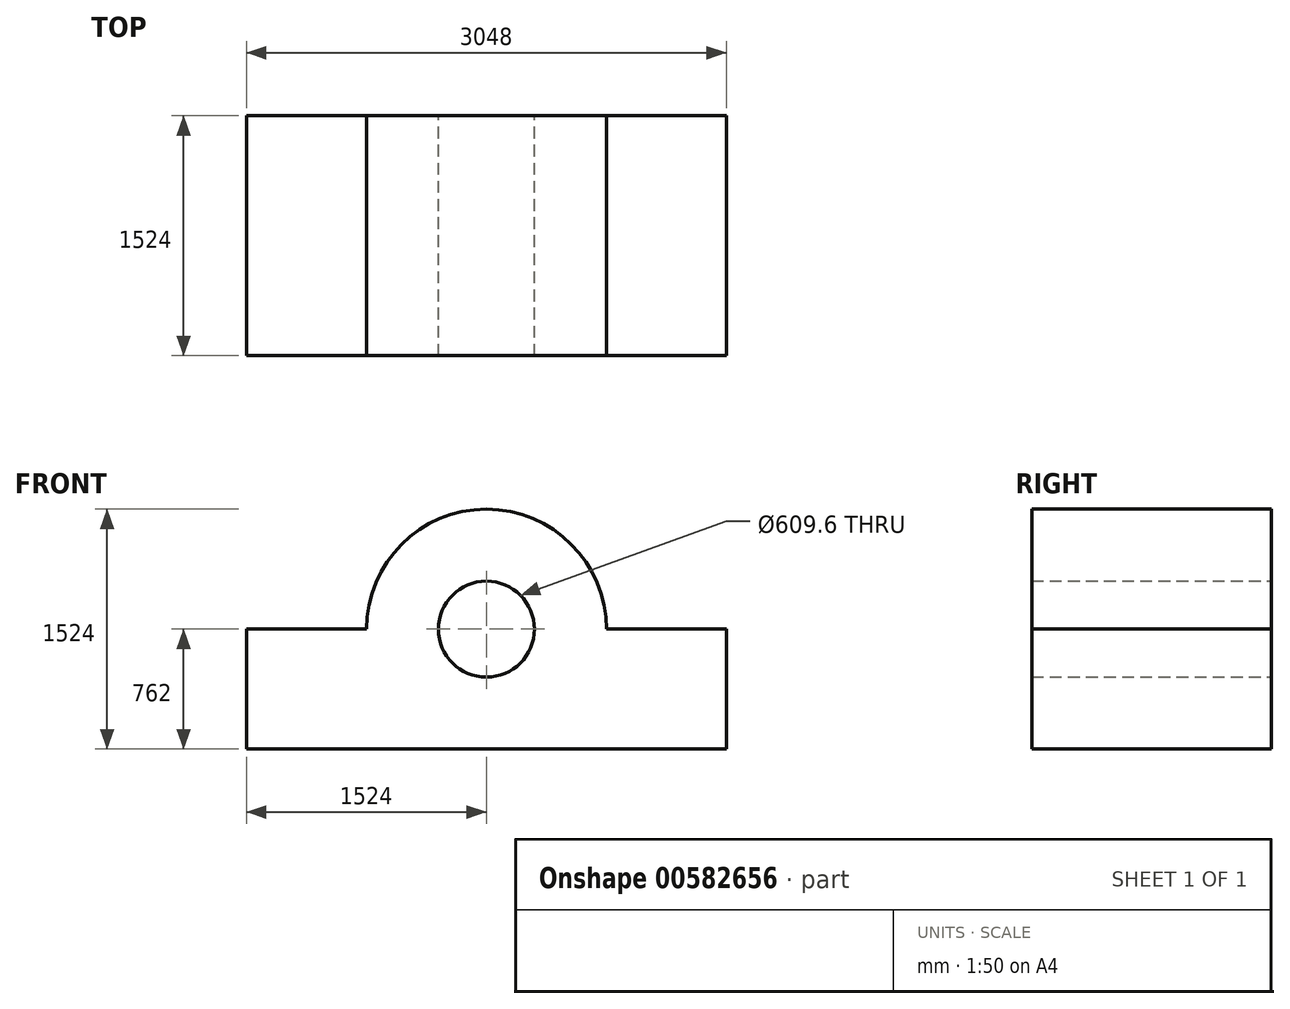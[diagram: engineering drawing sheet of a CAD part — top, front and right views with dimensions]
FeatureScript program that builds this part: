
annotation { "Feature Type Name" : "Feature", "Feature Type Description" : "" }
export const myFeature = defineFeature(function(context is Context, id is Id, definition is map)
    precondition{}
    {
        {
            var Q0;
            Q0=qCreatedBy(makeId("Front.planeOp"),FACE);
            var sketch = newSketch(context, id + "F0", { "sketchPlane" : qUnion([Q0])});
            skLineSegment(sketch, "E0", {"start": v(0, 0) * mm, "end": v(3048, 0) * mm});
            skLineSegment(sketch, "E1", {"start": v(3048, 0) * mm, "end": v(3048, 762) * mm});
            skLineSegment(sketch, "E2", {"start": v(3048, 762) * mm, "end": v(2286, 762) * mm});
            skCircle(sketch, "E3", {"center": v(1524, 762) * mm, "radius": 304.8 * mm});
            skArc(sketch, "E4", {"start": v(2286, 762) * mm, "mid": v(1524, 1524) * mm, "end": v(762, 762) * mm});
            skLineSegment(sketch, "E5", {"start": v(0, 0) * mm, "end": v(0, 762) * mm});
            skLineSegment(sketch, "E6", {"start": v(0, 762) * mm, "end": v(762, 762) * mm});
            skSolve(sketch);
        }
        {
            var Q0;
            Q0=makeQuery(id+"F0.imprint","IMPRINT",FACE,{"disambiguationData":[TD([[makeQuery(id+"F0.imprint","IMPRINT",EDGE,{"derivedFrom":sQuery(id+"F0.wireOp",EDGE,"E0")}),1.0]])]});
            extrude(context, id + "F1", {"entities" : qUnion([Q0]), "depth" : 1524 * mm, "offsetDistance" : 25.4 * mm});
        }
    });
